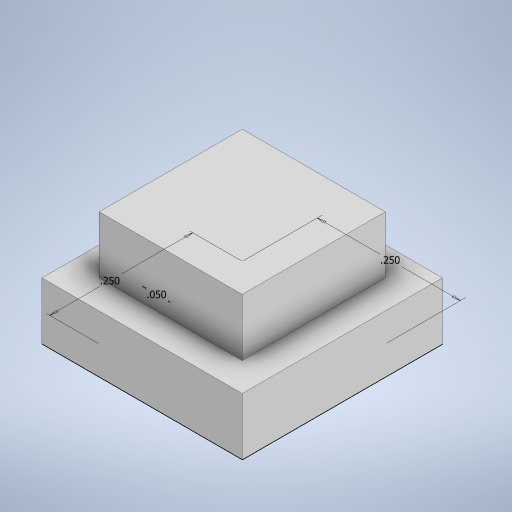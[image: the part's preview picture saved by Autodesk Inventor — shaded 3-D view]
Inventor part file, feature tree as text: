
AUTODESK INVENTOR PART (.ipt)
format: ipt  version: 2023 (Build 270158000, 158)  size: 224,768 bytes
history: native  units: in
note: dims shown in document units (in); Inventor stores cm internally (conversion verified against a paired STEP export)
features: extrude x2, sketch x1
ambient origin geometry x8: Origin, YZ Plane, XZ Plane, XY Plane, X Axis, Y Axis, Z Axis, Center Point
bodies: Solid1 (feature_tree)
feature tree (3):
  sketch  "Sketch1"  dims[d0=0.25in d1=0.25in d2=0.05in d3=0.2in d4=0.0in d5=0.1in d6=0.0in]
  extrude  "Extrusion1"  Depth=0.25in
  extrude  "Extrusion2"  Depth=0.05in
